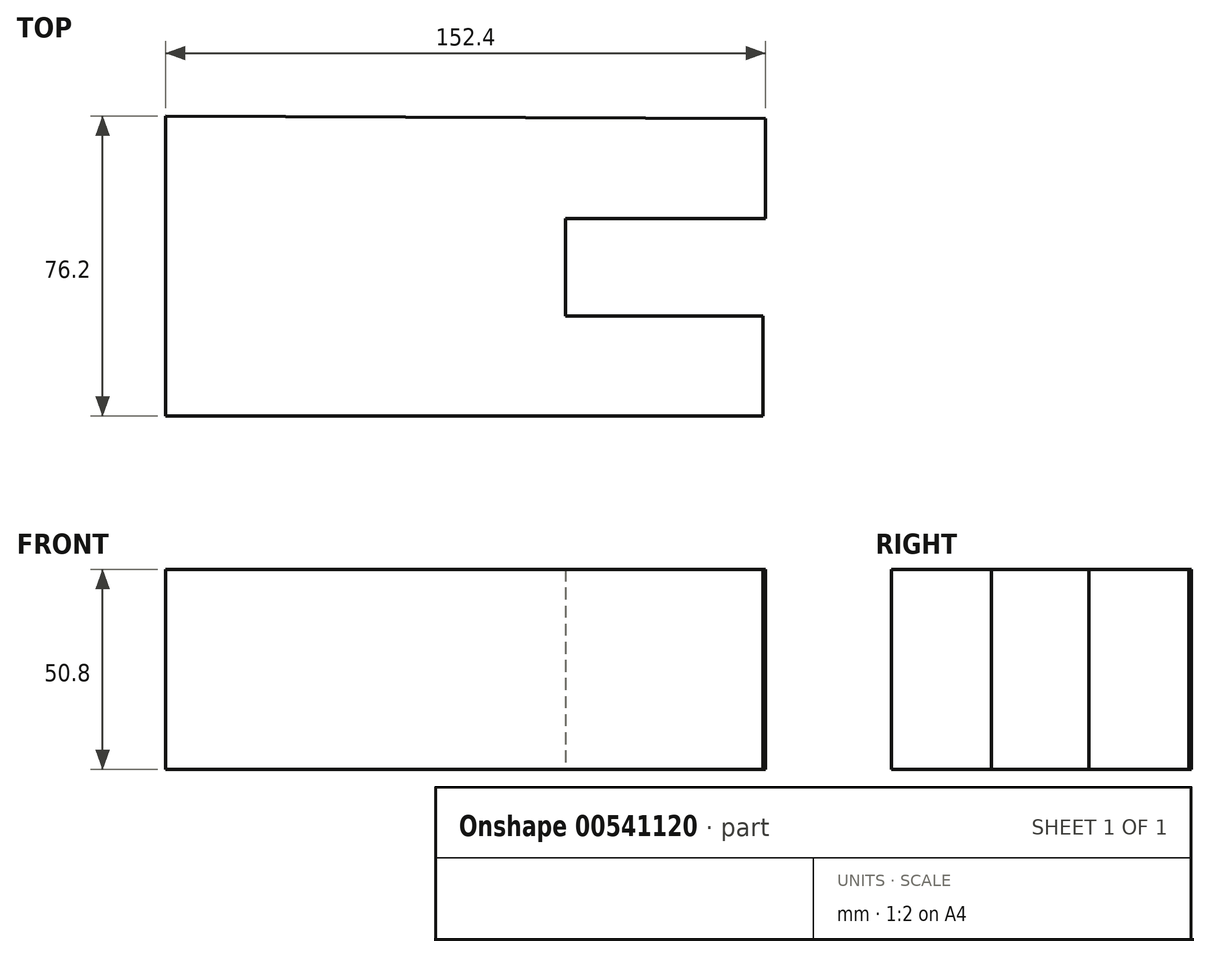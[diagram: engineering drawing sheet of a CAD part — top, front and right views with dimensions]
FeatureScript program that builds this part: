
annotation { "Feature Type Name" : "Feature", "Feature Type Description" : "" }
export const myFeature = defineFeature(function(context is Context, id is Id, definition is map)
    precondition{}
    {
        {
            var Q0;
            Q0=qCreatedBy(makeId("Top.planeOp"),FACE);
            var sketch = newSketch(context, id + "F0", { "sketchPlane" : qUnion([Q0])});
            skLineSegment(sketch, "E0", {"start": v(-81.99, 78.6) * mm, "end": v(70.4, 77.98) * mm});
            skLineSegment(sketch, "E1", {"start": v(70.4, 77.98) * mm, "end": v(70.4, 52.58) * mm});
            skLineSegment(sketch, "E2", {"start": v(70.4, 52.58) * mm, "end": v(19.6, 52.58) * mm});
            skLineSegment(sketch, "E3", {"start": v(19.6, 52.58) * mm, "end": v(19.6, 27.8) * mm});
            skLineSegment(sketch, "E4", {"start": v(19.6, 27.8) * mm, "end": v(69.82, 27.8) * mm});
            skLineSegment(sketch, "E5", {"start": v(69.82, 27.8) * mm, "end": v(69.82, 2.4) * mm});
            skLineSegment(sketch, "E6", {"start": v(69.82, 2.4) * mm, "end": v(-81.99, 2.4) * mm});
            skLineSegment(sketch, "E7", {"start": v(-81.99, 2.4) * mm, "end": v(-81.99, 78.6) * mm});
            skSolve(sketch);
        }
        {
            var Q0;
            Q0 = qSketchRegion(id + "F0", true);
            extrude(context, id + "F1", {"entities" : qUnion([Q0]), "depth" : 50.8 * mm, "offsetDistance" : 25.4 * mm});
        }
    });
